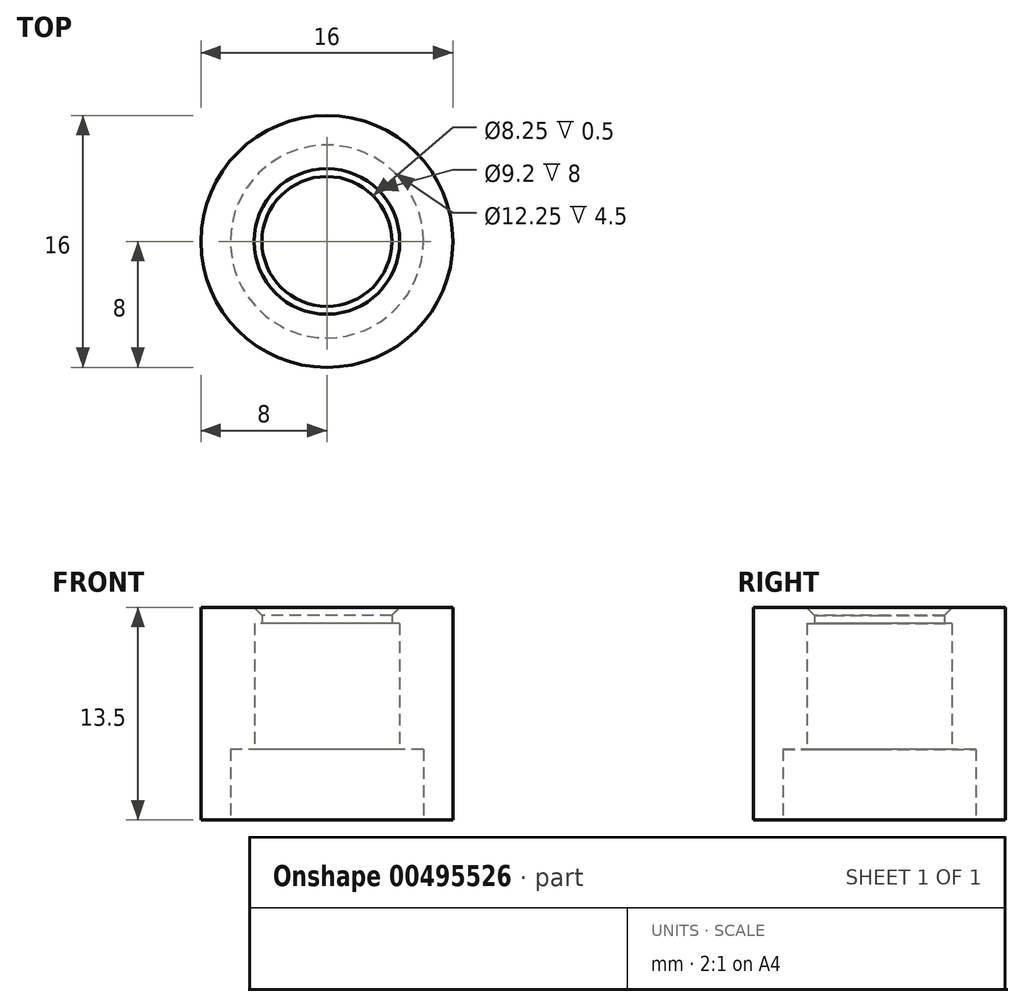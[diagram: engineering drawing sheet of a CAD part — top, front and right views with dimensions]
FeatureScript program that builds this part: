
annotation { "Feature Type Name" : "Feature", "Feature Type Description" : "" }
export const myFeature = defineFeature(function(context is Context, id is Id, definition is map)
    precondition{}
    {
        {
            var Q0;
            Q0=qCreatedBy(makeId("Top.planeOp"),FACE);
            var sketch = newSketch(context, id + "F0", { "sketchPlane" : qUnion([Q0])});
            skCircle(sketch, "E0", {"center": v(0, 0) * mm, "radius": 8 * mm});
            skCircle(sketch, "E1", {"center": v(0, 0) * mm, "radius": 4.12 * mm});
            skSolve(sketch);
        }
        {
            var Q0;
            Q0=makeQuery(id+"F0.imprint","IMPRINT",FACE,{"disambiguationData":[TD([[makeQuery(id+"F0.imprint","IMPRINT",EDGE,{"derivedFrom":sQuery(id+"F0.wireOp",EDGE,"E0")}),1.0]])]});
            extrude(context, id + "F1", {"entities" : qUnion([Q0]), "depth" : 13.5 * mm});
        }
        {
            var Q0;
            Q0=qCreatedBy(makeId("Top.planeOp"),FACE);
            var sketch = newSketch(context, id + "F2", { "sketchPlane" : qUnion([Q0])});
            skCircle(sketch, "E2", {"center": v(0, 0) * mm, "radius": 4.6 * mm});
            skSolve(sketch);
        }
        {
            var Q0;
            Q0 = qSketchRegion(id + "F2", true);
            extrude(context, id + "F3", {"entities" : qUnion([Q0]), "operationType" : NewBodyOperationType.REMOVE, "depth" : 12.5 * mm});
        }
        {
            var Q0;
            Q0=qCreatedBy(makeId("Top.planeOp"),FACE);
            var sketch = newSketch(context, id + "F4", { "sketchPlane" : qUnion([Q0])});
            skCircle(sketch, "E3", {"center": v(0, 0) * mm, "radius": 6.12 * mm});
            skSolve(sketch);
        }
        {
            var Q0;
            Q0 = qSketchRegion(id + "F4", true);
            extrude(context, id + "F5", {"entities" : qUnion([Q0]), "operationType" : NewBodyOperationType.REMOVE, "depth" : 4.5 * mm});
        }
        {
            var Q0;
            Q0=makeQuery(id+"F1.opExtrude","CAP_EDGE",EDGE,{"disambiguationData":[OSD([sQuery(id+"F0.wireOp",EDGE,"E1")])],"isStart":false});
            chamfer(context, id + "F6", {"entities" : qUnion([Q0]), "width" : 0.5 * mm, "tangentPropagation" : true});
        }
    });
